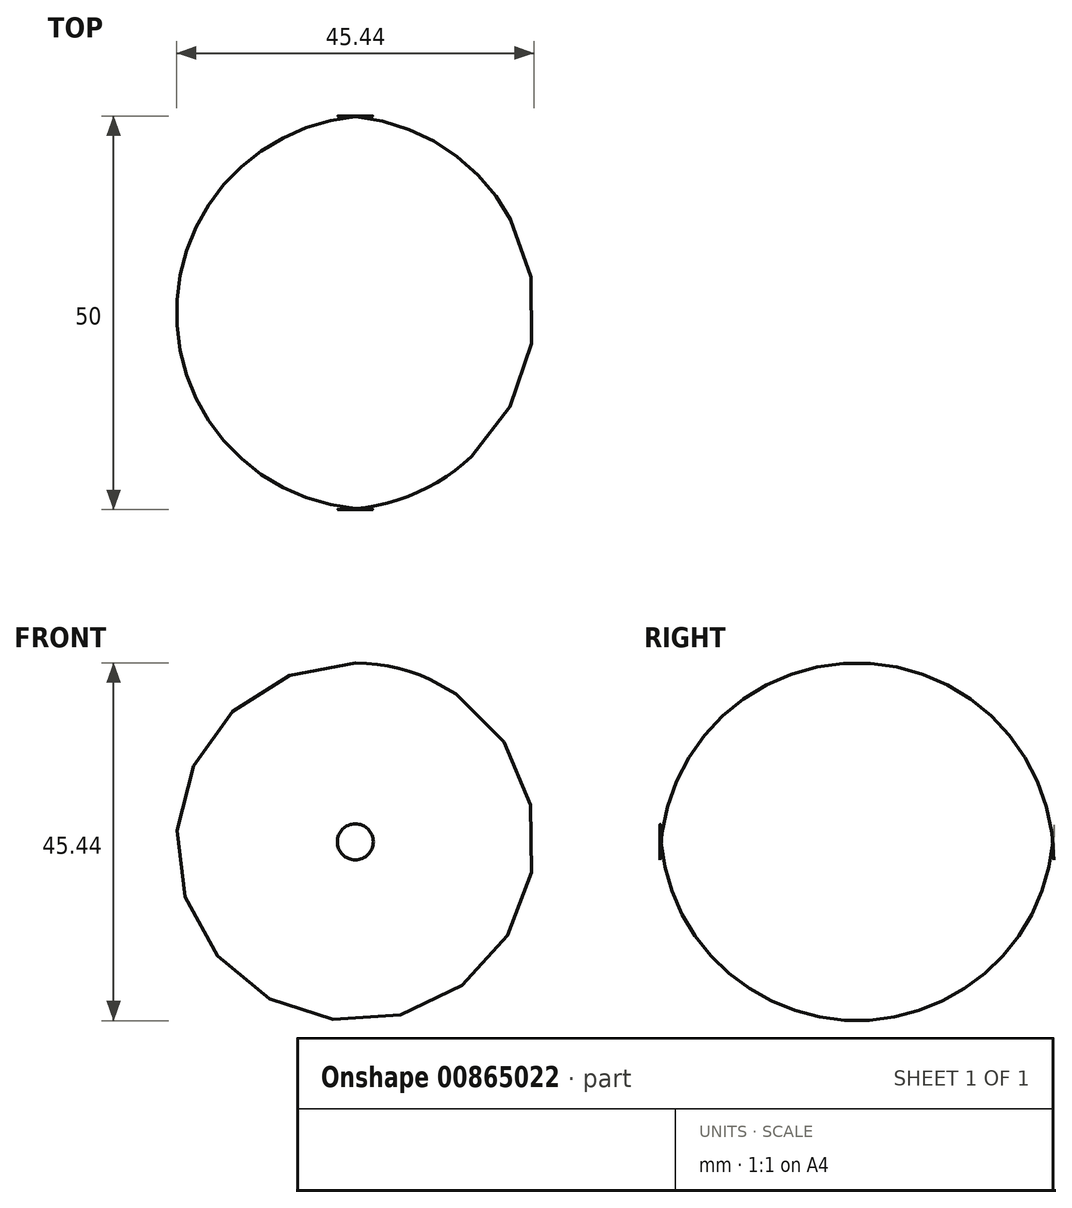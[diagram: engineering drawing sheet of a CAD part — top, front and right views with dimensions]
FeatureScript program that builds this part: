
annotation { "Feature Type Name" : "Feature", "Feature Type Description" : "" }
export const myFeature = defineFeature(function(context is Context, id is Id, definition is map)
    precondition{}
    {
        {
            var Q0;
            Q0=qCreatedBy(makeId("Front.planeOp"),FACE);
            var sketch = newSketch(context, id + "F0", { "sketchPlane" : qUnion([Q0])});
            skCircle(sketch, "E0", {"center": v(0, 0) * mm, "radius": 27.28 * mm});
            skSolve(sketch);
        }
        {
            var Q0;
            Q0=makeQuery(id+"F0.imprint","IMPRINT",FACE,{"disambiguationData":[TD([[makeQuery(id+"F0.imprint","IMPRINT",EDGE,{"derivedFrom":sQuery(id+"F0.wireOp",EDGE,"E0")}),1.0]])]});
            extrude(context, id + "F1", {"entities" : qUnion([Q0]), "depth" : 25 * mm, "offsetDistance" : 25 * mm});
        }
        {
            var Q0;
            Q0=makeQuery(id+"F1.opExtrude","CAP_EDGE",EDGE,{"disambiguationData":[OSD([sQuery(id+"F0.wireOp",EDGE,"E0")])],"isStart":true});
            fillet(context, id + "F2", {"entities" : qUnion([Q0]), "radius" : 25 * mm, "tangentPropagation" : true, "allowEdgeOverflow" : false});
        }
        {
            var Q0;
            Q0=makeQuery(id+"F1.opExtrude","CAP_FACE",FACE,{"disambiguationData":[OSD([sQuery(id+"F0.wireOp",EDGE,"E0")])],"isStart":false});
            extrude(context, id + "F3", {"entities" : qUnion([Q0]), "operationType" : NewBodyOperationType.ADD, "depth" : 25 * mm, "offsetDistance" : 25 * mm});
        }
        {
            var Q0;
            Q0=makeQuery(id+"F3.opExtrude","CAP_EDGE",EDGE,{"disambiguationData":[OSD([sQuery(id+"F0.wireOp",EDGE,"E0")])],"isStart":false});
            fillet(context, id + "F4", {"entities" : qUnion([Q0]), "radius" : 25 * mm, "tangentPropagation" : true, "allowEdgeOverflow" : false});
        }
    });
